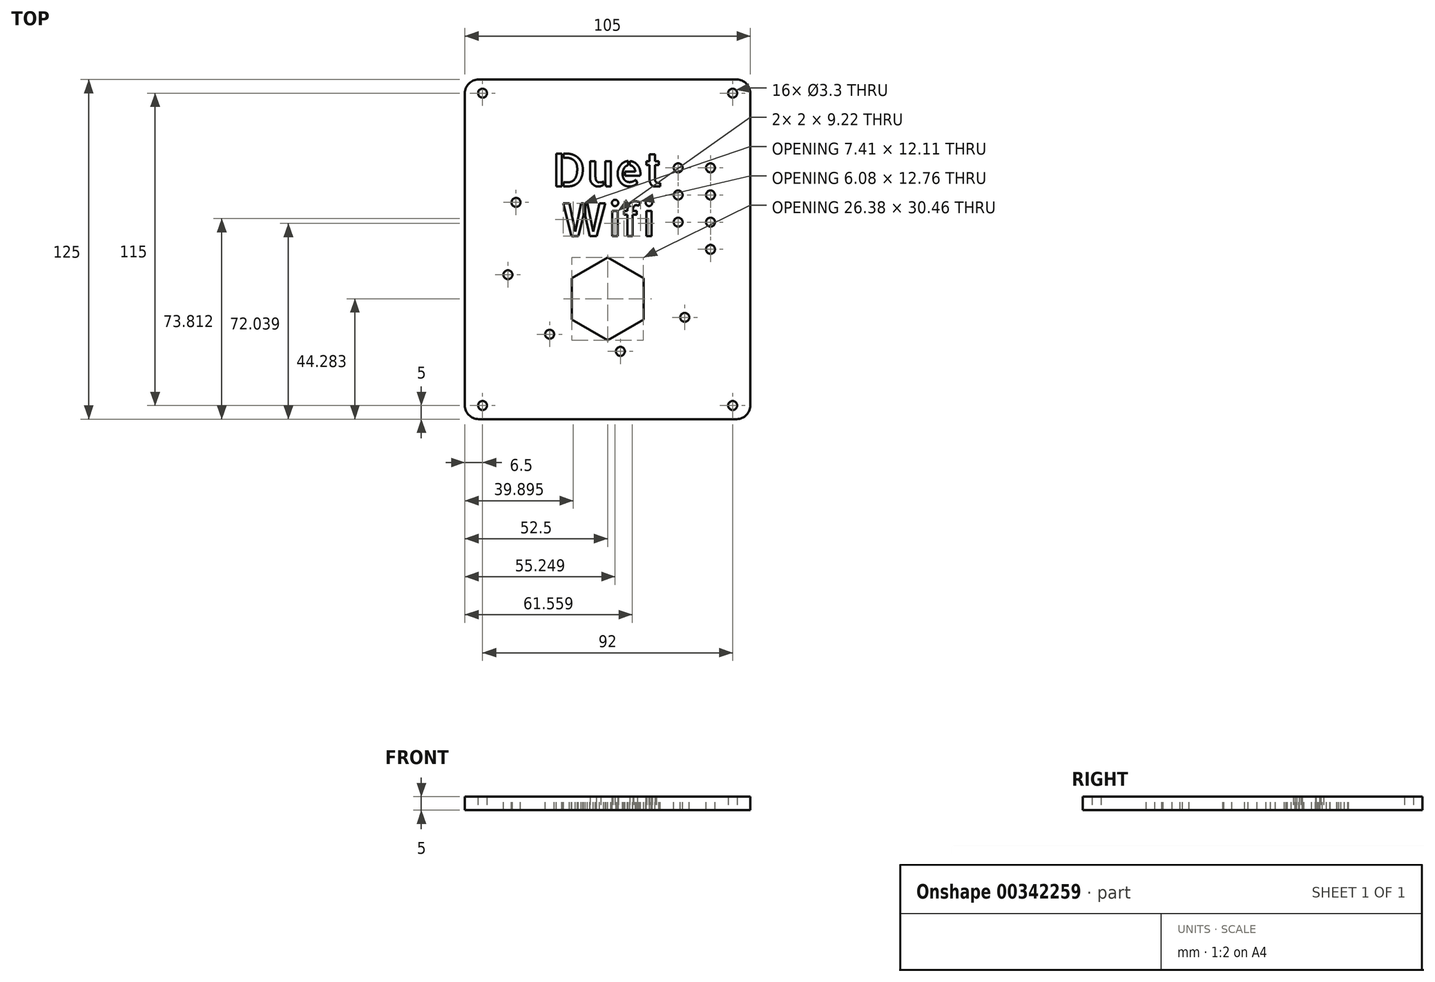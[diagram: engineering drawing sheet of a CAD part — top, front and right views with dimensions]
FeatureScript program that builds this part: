
annotation { "Feature Type Name" : "Feature", "Feature Type Description" : "" }
export const myFeature = defineFeature(function(context is Context, id is Id, definition is map)
    precondition{}
    {
        {
            var Q0;
            Q0=qCreatedBy(makeId("Top.planeOp"),FACE);
            var sketch = newSketch(context, id + "F0", { "sketchPlane" : qUnion([Q0])});
            skLineSegment(sketch, "E0.bottom", {"start": v(-52.5, 62.5) * mm, "end": v(52.5, 62.5) * mm});
            skLineSegment(sketch, "E0.top", {"start": v(-52.5, -62.5) * mm, "end": v(52.5, -62.5) * mm});
            skLineSegment(sketch, "E0.left", {"start": v(-52.5, 62.5) * mm, "end": v(-52.5, -62.5) * mm});
            skLineSegment(sketch, "E0.right", {"start": v(52.5, 62.5) * mm, "end": v(52.5, -62.5) * mm});
            skPoint(sketch, "E0.middle", {"position": v(0, 0) * mm});
            skLineSegment(sketch, "E1.bottom", {"start": v(46, 57.5) * mm, "end": v(-46, 57.5) * mm, "construction": true});
            skLineSegment(sketch, "E1.top", {"start": v(46, -57.5) * mm, "end": v(-46, -57.5) * mm, "construction": true});
            skLineSegment(sketch, "E1.left", {"start": v(46, 57.5) * mm, "end": v(46, -57.5) * mm, "construction": true});
            skLineSegment(sketch, "E1.right", {"start": v(-46, 57.5) * mm, "end": v(-46, -57.5) * mm, "construction": true});
            skSolve(sketch);
        }
        {
            var Q0;
            Q0 = qSketchRegion(id + "F0", true);
            extrude(context, id + "F1", {"entities" : qUnion([Q0]), "depth" : 5 * mm});
        }
        {
            var Q0;
            Q0=sQuery(id+"F0.wireOp",VERTEX,"E1.right.start");
            var Q1;
            Q1=sQuery(id+"F0.wireOp",VERTEX,"E1.left.start");
            var Q2;
            Q2=sQuery(id+"F0.wireOp",VERTEX,"E1.left.end");
            var Q3;
            Q3=sQuery(id+"F0.wireOp",VERTEX,"E1.right.end");
            var Q4;
            Q4=makeQuery(id+"F1.opExtrude","SWEPT_BODY",BODY,{"disambiguationData":[OSD([sQuery(id+"F0.wireOp",EDGE,"E0.bottom"),sQuery(id+"F0.wireOp",EDGE,"E0.top"),sQuery(id+"F0.wireOp",EDGE,"E0.left"),sQuery(id+"F0.wireOp",EDGE,"E0.right")])]});
            hole(context, id + "F2", {"style" : HoleStyle.SIMPLE, "endStyle" : HoleEndStyle.THROUGH, "oppositeDirection" : true, "standardTappedOrClearance" : lookupTablePath({ "standard" : "ISO", "fit" : "Normal", "size" : "M3", "type" : "Clearance" }), "standardBlindInLast" : lookupTablePath({ "fit" : "Standard", "standard" : "ISO", "size" : "M3", "type" : "Clearance" }), "holeDiameter" : 3.3 * mm, "isTappedThrough" : true, "tappedDepth" : 12 * mm, "tapClearance" : 3, "startFromSketch" : true, "locations" : qUnion([Q0, Q1, Q2, Q3]), "scope" : qUnion([Q4])});
        }
        {
            var Q0;
            Q0=makeQuery(id+"F1.opExtrude","SWEPT_EDGE",EDGE,{"disambiguationData":[OSD([sQuery(id+"F0.wireOp",EDGE,"E0.bottom"),sQuery(id+"F0.wireOp",EDGE,"E0.left")])]});
            var Q1;
            Q1=makeQuery(id+"F1.opExtrude","SWEPT_EDGE",EDGE,{"disambiguationData":[OSD([sQuery(id+"F0.wireOp",EDGE,"E0.bottom"),sQuery(id+"F0.wireOp",EDGE,"E0.right")])]});
            var Q2;
            Q2=makeQuery(id+"F1.opExtrude","SWEPT_EDGE",EDGE,{"disambiguationData":[OSD([sQuery(id+"F0.wireOp",EDGE,"E0.top"),sQuery(id+"F0.wireOp",EDGE,"E0.right")])]});
            var Q3;
            Q3=makeQuery(id+"F1.opExtrude","SWEPT_EDGE",EDGE,{"disambiguationData":[OSD([sQuery(id+"F0.wireOp",EDGE,"E0.top"),sQuery(id+"F0.wireOp",EDGE,"E0.left")])]});
            fillet(context, id + "F3", {"entities" : qUnion([Q0, Q1, Q2, Q3]), "radius" : 5 * mm, "tangentPropagation" : true, "allowEdgeOverflow" : false});
        }
        {
            var Q0;
            Q0=makeQuery(id+"F1.opExtrude","CAP_FACE",FACE,{"disambiguationData":[OSD([sQuery(id+"F0.wireOp",EDGE,"E0.bottom"),sQuery(id+"F0.wireOp",EDGE,"E0.top"),sQuery(id+"F0.wireOp",EDGE,"E0.left"),sQuery(id+"F0.wireOp",EDGE,"E0.right")])],"isStart":false});
            var sketch = newSketch(context, id + "F4", { "sketchPlane" : qUnion([Q0])});
            skText(sketch, "E2", { "text": "Duet", "fontName": "AllertaStencil-Regular.ttf"});
            skText(sketch, "E3", { "text": "Wifi", "fontName": "AllertaStencil-Regular.ttf"});
            skPoint(sketch, "E4", {"position": v(37.86, 0) * mm});
            skPoint(sketch, "E5.1.0", {"position": v(28.38, -25.05) * mm});
            skPoint(sketch, "E5.2.0", {"position": v(4.7, -37.56) * mm});
            skPoint(sketch, "E5.3.0", {"position": v(-21.33, -31.28) * mm});
            skPoint(sketch, "E5.4.0", {"position": v(-36.69, -9.34) * mm});
            skPoint(sketch, "E5.5.0", {"position": v(-33.69, 17.27) * mm});
            skPoint(sketch, "E5.6.0", {"position": v(-13.83, 35.24) * mm});
            skPoint(sketch, "E5.7.0", {"position": v(12.95, 35.57) * mm});
            skPoint(sketch, "E5.center", {"position": v(0, 0) * mm});
            skLineSegment(sketch, "E5.anchor1", {"start": v(0, 0) * mm, "end": v(37.86, 0) * mm, "construction": true});
            skLineSegment(sketch, "E5.anchor2", {"start": v(0, 0) * mm, "end": v(12.95, 35.57) * mm, "construction": true});
            skPoint(sketch, "E6.0.1.0", {"position": v(37.86, 10) * mm});
            skPoint(sketch, "E6.0.2.0", {"position": v(37.86, 20) * mm});
            skPoint(sketch, "E6.0.3.0", {"position": v(37.86, 30) * mm});
            skPoint(sketch, "E6.1.0.0", {"position": v(25.96, 0) * mm});
            skPoint(sketch, "E6.1.1.0", {"position": v(25.96, 10) * mm});
            skPoint(sketch, "E6.1.2.0", {"position": v(25.96, 20) * mm});
            skPoint(sketch, "E6.1.3.0", {"position": v(25.96, 30) * mm});
            skPoint(sketch, "E6.2.0.0", {"position": v(14.06, 0) * mm});
            skPoint(sketch, "E6.2.1.0", {"position": v(14.06, 10) * mm});
            skPoint(sketch, "E6.2.2.0", {"position": v(14.06, 20) * mm});
            skPoint(sketch, "E6.2.3.0", {"position": v(14.06, 30) * mm});
            skLineSegment(sketch, "E6.direction1", {"start": v(37.86, 0) * mm, "end": v(25.96, 0) * mm, "construction": true});
            skLineSegment(sketch, "E6.direction2", {"start": v(37.86, 0) * mm, "end": v(37.86, 10) * mm, "construction": true});
            const initialGuessF4  = {"E2": [-0.02041, 0.0232, 1, 0, 0.01205], "E3": [-0.0175, 0.00493, 1, 0, 0.01205]};
            skSetInitialGuess(sketch, initialGuessF4);
            skSolve(sketch);
        }
        {
            var Q0;
            Q0 = qSketchRegion(id + "F4", true);
            extrude(context, id + "F5", {"entities" : qUnion([Q0]), "operationType" : NewBodyOperationType.REMOVE, "oppositeDirection" : true, "depth" : 25 * mm});
        }
        {
            var Q0;
            Q0=sQuery(id+"F4.wireOp",VERTEX,"E5.5.0");
            var Q1;
            Q1=sQuery(id+"F4.wireOp",VERTEX,"E5.4.0");
            var Q2;
            Q2=sQuery(id+"F4.wireOp",VERTEX,"E5.3.0");
            var Q3;
            Q3=sQuery(id+"F4.wireOp",VERTEX,"E5.2.0");
            var Q4;
            Q4=sQuery(id+"F4.wireOp",VERTEX,"E5.1.0");
            var Q5;
            Q5=sQuery(id+"F4.wireOp",VERTEX,"E4");
            var Q6;
            Q6=sQuery(id+"F4.wireOp",VERTEX,"E6.1.1.0");
            var Q7;
            Q7=sQuery(id+"F4.wireOp",VERTEX,"E6.0.1.0");
            var Q8;
            Q8=sQuery(id+"F4.wireOp",VERTEX,"E6.1.3.0");
            var Q9;
            Q9=sQuery(id+"F4.wireOp",VERTEX,"E6.0.3.0");
            var Q10;
            Q10=sQuery(id+"F4.wireOp",VERTEX,"E6.0.2.0");
            var Q11;
            Q11=sQuery(id+"F4.wireOp",VERTEX,"E6.1.2.0");
            var Q12;
            Q12=makeQuery(id+"F1.opExtrude","SWEPT_BODY",BODY,{"disambiguationData":[OSD([sQuery(id+"F0.wireOp",EDGE,"E0.bottom"),sQuery(id+"F0.wireOp",EDGE,"E0.top"),sQuery(id+"F0.wireOp",EDGE,"E0.left"),sQuery(id+"F0.wireOp",EDGE,"E0.right")])]});
            hole(context, id + "F6", {"style" : HoleStyle.SIMPLE, "endStyle" : HoleEndStyle.THROUGH, "standardTappedOrClearance" : lookupTablePath({ "standard" : "ISO", "fit" : "Normal", "size" : "M3", "type" : "Clearance" }), "standardBlindInLast" : lookupTablePath({ "fit" : "Standard", "standard" : "ISO", "size" : "M3", "type" : "Clearance" }), "holeDiameter" : 3.3 * mm, "isTappedThrough" : true, "tappedDepth" : 12 * mm, "tapClearance" : 3, "startFromSketch" : true, "locations" : qUnion([Q0, Q1, Q2, Q3, Q4, Q5, Q6, Q7, Q8, Q9, Q10, Q11]), "scope" : qUnion([Q12])});
        }
        {
            var Q0;
            Q0=makeQuery(id+"F4.imprint","IMPRINT",FACE,{"disambiguationData":[TD([[makeQuery(id+"F4.imprint","IMPRINT",EDGE,{"derivedFrom":sQuery(id+"F4.wireOp",EDGE,"E2.sketch_text.stroke-0")}),1.0]])]});
            var sketch = newSketch(context, id + "F7", { "sketchPlane" : qUnion([Q0])});
            skLineSegment(sketch, "E7", {"start": v(-40.13, 49.9) * mm, "end": v(41.08, 49.9) * mm});
            skLineSegment(sketch, "E8", {"start": v(41.08, 49.9) * mm, "end": v(41.08, 36.24) * mm});
            skLineSegment(sketch, "E9", {"start": v(41.08, 36.24) * mm, "end": v(0.47, 49.9) * mm});
            skLineSegment(sketch, "E10", {"start": v(0.47, 49.9) * mm, "end": v(-40.13, 36.24) * mm});
            skLineSegment(sketch, "E11", {"start": v(-40.13, 36.24) * mm, "end": v(-40.13, 49.9) * mm});
            skLineSegment(sketch, "E12.MirrorCS", {"start": v(-40.13, -49.9) * mm, "end": v(41.08, -49.9) * mm});
            skLineSegment(sketch, "E13.MirrorCS", {"start": v(-40.13, -36.24) * mm, "end": v(-40.13, -49.9) * mm});
            skLineSegment(sketch, "E14.MirrorCS", {"start": v(0.47, -49.9) * mm, "end": v(-40.13, -36.24) * mm});
            skLineSegment(sketch, "E15.MirrorCS", {"start": v(41.08, -36.24) * mm, "end": v(0.47, -49.9) * mm});
            skLineSegment(sketch, "E16.MirrorCS", {"start": v(41.08, -49.9) * mm, "end": v(41.08, -36.24) * mm});
            skCircle(sketch, "E17.cCircle", {"center": v(0, -18.22) * mm, "radius": 13.19 * mm, "construction": true});
            skLineSegment(sketch, "E17.0", {"start": v(13.19, -10.6) * mm, "end": v(13.19, -25.83) * mm});
            skLineSegment(sketch, "E17.1", {"start": v(13.19, -25.83) * mm, "end": v(0, -33.45) * mm});
            skLineSegment(sketch, "E17.2", {"start": v(0, -33.45) * mm, "end": v(-13.19, -25.83) * mm});
            skLineSegment(sketch, "E17.3", {"start": v(-13.19, -25.83) * mm, "end": v(-13.19, -10.6) * mm});
            skLineSegment(sketch, "E17.4", {"start": v(-13.19, -10.6) * mm, "end": v(0, -2.99) * mm});
            skLineSegment(sketch, "E17.5", {"start": v(0, -2.99) * mm, "end": v(13.19, -10.6) * mm});
            skPoint(sketch, "E17.0.midPoint", {"position": v(13.19, -18.22) * mm});
            skSolve(sketch);
        }
        {
            var Q0;
            Q0=makeQuery(id+"F7.imprint","IMPRINT",FACE,{"disambiguationData":[TD([[makeQuery(id+"F7.imprint","IMPRINT",EDGE,{"derivedFrom":sQuery(id+"F7.wireOp",EDGE,"E17.0")}),-1.0]])]});
            extrude(context, id + "F8", {"entities" : qUnion([Q0]), "operationType" : NewBodyOperationType.REMOVE, "oppositeDirection" : true, "depth" : 25 * mm});
        }
    });
